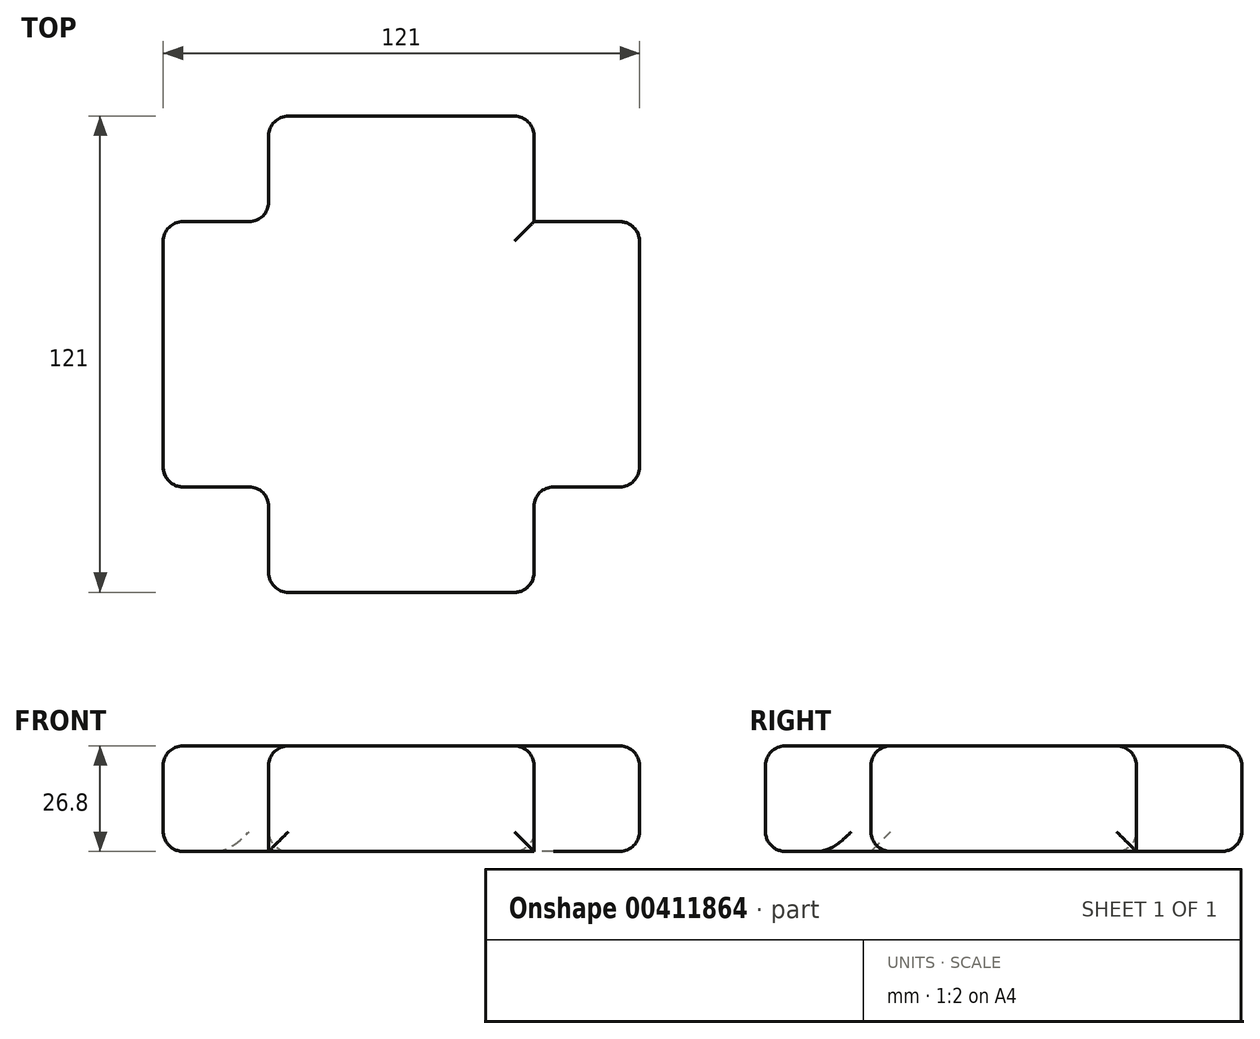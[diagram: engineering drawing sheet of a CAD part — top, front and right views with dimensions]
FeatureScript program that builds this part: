
annotation { "Feature Type Name" : "Feature", "Feature Type Description" : "" }
export const myFeature = defineFeature(function(context is Context, id is Id, definition is map)
    precondition{}
    {
        {
            var Q0;
            Q0=qCreatedBy(makeId("Top.planeOp"),FACE);
            var sketch = newSketch(context, id + "F0", { "sketchPlane" : qUnion([Q0])});
            skLineSegment(sketch, "E0.bottom", {"start": v(-38.33, 39.37) * mm, "end": v(55.87, 39.37) * mm});
            skLineSegment(sketch, "E0.top", {"start": v(-38.33, -81.63) * mm, "end": v(82.67, -81.63) * mm});
            skLineSegment(sketch, "E0.left", {"start": v(-38.33, 39.37) * mm, "end": v(-38.33, -81.63) * mm});
            skLineSegment(sketch, "E0.right", {"start": v(82.67, 39.37) * mm, "end": v(82.67, -81.63) * mm});
            skLineSegment(sketch, "E1.top", {"start": v(-38.33, 12.57) * mm, "end": v(-11.53, 12.57) * mm});
            skLineSegment(sketch, "E1.right", {"start": v(-11.53, 39.37) * mm, "end": v(-11.53, 12.57) * mm});
            skLineSegment(sketch, "E2.top", {"start": v(-38.33, -54.83) * mm, "end": v(-11.53, -54.83) * mm});
            skLineSegment(sketch, "E2.right", {"start": v(-11.53, -81.63) * mm, "end": v(-11.53, -54.83) * mm});
            skLineSegment(sketch, "E3.top", {"start": v(82.67, -54.83) * mm, "end": v(55.87, -54.83) * mm});
            skLineSegment(sketch, "E3.right", {"start": v(55.87, -81.63) * mm, "end": v(55.87, -54.83) * mm});
            skLineSegment(sketch, "E4.bottom", {"start": v(82.67, 39.37) * mm, "end": v(55.87, 39.37) * mm});
            skLineSegment(sketch, "E4.top", {"start": v(82.67, 12.57) * mm, "end": v(55.87, 12.57) * mm});
            skLineSegment(sketch, "E4.right", {"start": v(55.87, 39.37) * mm, "end": v(55.87, 12.57) * mm});
            skSolve(sketch);
        }
        {
            var Q0;
            {var subQ3=sQuery(id+"F0.wireOp",EDGE,"E1.top");Q0=makeQuery(id+"F0.imprint","IMPRINT",FACE,{"disambiguationData":[TD([[makeQuery(id+"F0.imprint","IMPRINT",EDGE,{"derivedFrom":subQ3}),-1.0]])]});}
            extrude(context, id + "F1", {"entities" : qUnion([Q0]), "depth" : 26.8 * mm});
        }
        {
            var Q0;
            Q0=makeQuery(id+"F1.opExtrude","CAP_FACE",FACE,{"disambiguationData":[OSD([sQuery(id+"F0.wireOp",EDGE,"E0.bottom"),sQuery(id+"F0.wireOp",EDGE,"E0.top"),sQuery(id+"F0.wireOp",EDGE,"E0.left"),sQuery(id+"F0.wireOp",EDGE,"E0.right"),sQuery(id+"F0.wireOp",EDGE,"E1.top"),sQuery(id+"F0.wireOp",EDGE,"E1.right"),sQuery(id+"F0.wireOp",EDGE,"E2.top"),sQuery(id+"F0.wireOp",EDGE,"E2.right"),sQuery(id+"F0.wireOp",EDGE,"E3.top"),sQuery(id+"F0.wireOp",EDGE,"E3.right"),sQuery(id+"F0.wireOp",EDGE,"E4.top"),sQuery(id+"F0.wireOp",EDGE,"E4.right")])],"isStart":false});
            var Q1;
            Q1=makeQuery(id+"F1.opExtrude","SWEPT_EDGE",EDGE,{"disambiguationData":[OSD([sQuery(id+"F0.wireOp",EDGE,"E0.top"),sQuery(id+"F0.wireOp",EDGE,"E3.right")])]});
            var Q2;
            Q2=makeQuery(id+"F1.opExtrude","SWEPT_EDGE",EDGE,{"disambiguationData":[OSD([sQuery(id+"F0.wireOp",EDGE,"E3.top"),sQuery(id+"F0.wireOp",EDGE,"E3.right")])]});
            var Q3;
            Q3=makeQuery(id+"F1.opExtrude","SWEPT_EDGE",EDGE,{"disambiguationData":[OSD([sQuery(id+"F0.wireOp",EDGE,"E0.right"),sQuery(id+"F0.wireOp",EDGE,"E3.top")])]});
            var Q4;
            Q4=makeQuery(id+"F1.opExtrude","SWEPT_FACE",FACE,{"disambiguationData":[OSD([sQuery(id+"F0.wireOp",EDGE,"E0.right")])]});
            var Q5;
            Q5=makeQuery(id+"F1.opExtrude","SWEPT_FACE",FACE,{"disambiguationData":[OSD([sQuery(id+"F0.wireOp",EDGE,"E0.top")])]});
            var Q6;
            Q6=makeQuery(id+"F1.opExtrude","SWEPT_EDGE",EDGE,{"disambiguationData":[OSD([sQuery(id+"F0.wireOp",EDGE,"E2.top"),sQuery(id+"F0.wireOp",EDGE,"E2.right")])]});
            var Q7;
            Q7=makeQuery(id+"F1.opExtrude","SWEPT_FACE",FACE,{"disambiguationData":[OSD([sQuery(id+"F0.wireOp",EDGE,"E3.top")])]});
            var Q8;
            Q8=makeQuery(id+"F1.opExtrude","SWEPT_FACE",FACE,{"disambiguationData":[OSD([sQuery(id+"F0.wireOp",EDGE,"E0.left")])]});
            var Q9;
            Q9=makeQuery(id+"F1.opExtrude","SWEPT_FACE",FACE,{"disambiguationData":[OSD([sQuery(id+"F0.wireOp",EDGE,"E1.right")])]});
            var Q10;
            Q10=makeQuery(id+"F1.opExtrude","SWEPT_FACE",FACE,{"disambiguationData":[OSD([sQuery(id+"F0.wireOp",EDGE,"E0.bottom")])]});
            fillet(context, id + "F2", {"entities" : qUnion([Q0, Q1, Q2, Q3, Q4, Q5, Q6, Q7, Q8, Q9, Q10]), "radius" : 5 * mm, "tangentPropagation" : true, "allowEdgeOverflow" : false});
        }
    });
